# Revit family: Sanitary_Dryers_(Hand_Hair)_Johnson-Suisse_Fuga_Hand_Dryer_White
name_source: partatom
category: Plumbing Fixtures
revit_build: Autodesk Revit 2015 (Build: 20140606_1530(x64)
units: mm (PartAtom-declared; Revit-internal decimal feet)

## types (1)
- Fuga Hand Dryer White
    BIMobject category = Dryers (Hand & Hair)
    Brand url = http://www.johnsonsuisse.com.au
    Design country = Spain
    EAN code = https://8435368833632
    Edition number = 1
    IFC Classification = Electric Appliance
    Manufacturer country = Spain
    Manufacturer name = Johnson Suisse
    Material main = ABS
    NBS Reference Code = 60-80
    NBS Reference Description = Drying Systems
    Nominal height = 328 mm  [stored 1.07612 ft]
    Nominal width = 255 mm  [stored 0.836614 ft]
    OmniClass Code = 23-31 25 15
    OmniClass Description = Hand Dryers
    Product Guid = bff8133c-6a20-46b4-8baa-70fc282a8793
    Product SKU = NHD01861-W
    Product data url = https://bimobject.com
    Product family = Nofer
    Product group = Hand & Hair Dryers
    Product url = https://johnsonsuisse.com.au
    QR code = http://bimobject.com
    Technical description = https://johnsonsuisse.com.au
    Type = fuga_hand_dryer_white : Default
    UNSPSC Code = 301815
    Uniclass 1.4 Code = L82421
    Uniclass 1.4 Description = Hand driers
    Uniclass 2.0 Code = SS-60-80
    Uniclass 2.0 Description = Drying Systems
    Uniclass 2015 Code = Pr_40_70_62_37
    Uniclass 2015 Name = Hand driers
    Weight Net (Kg) = 3.6

note: [stored X ft] marks values corroborated as IEEE doubles in the binary element streams (Revit-internal decimal feet)

## geometry (parser evidence)
native form markers: Sweep x6
no freeform markers — native parametric forms only
